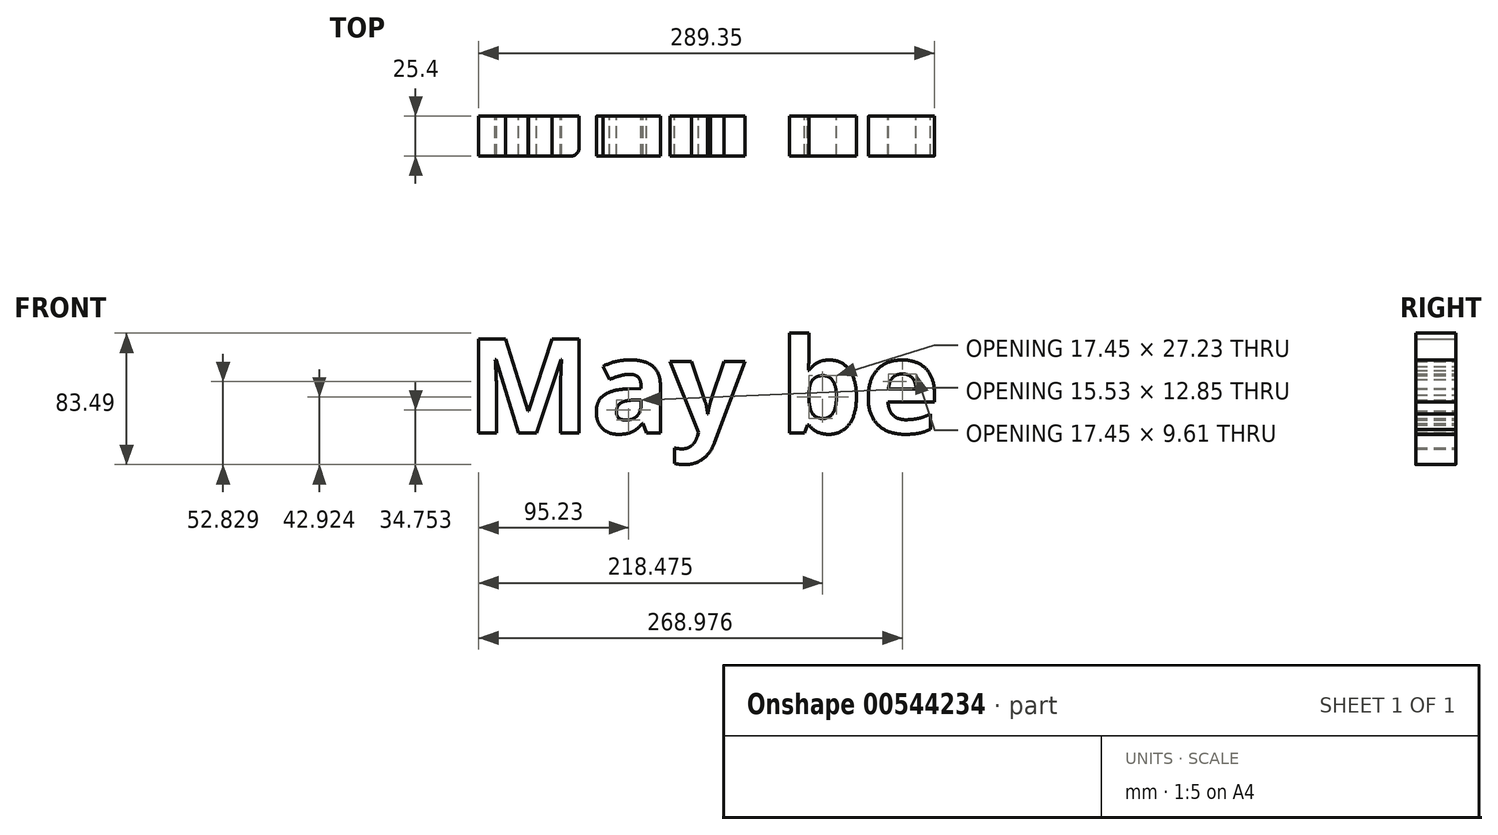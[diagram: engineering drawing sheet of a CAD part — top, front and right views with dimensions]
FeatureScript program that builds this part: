
annotation { "Feature Type Name" : "Feature", "Feature Type Description" : "" }
export const myFeature = defineFeature(function(context is Context, id is Id, definition is map)
    precondition{}
    {
        {
            var Q0;
            Q0=qCreatedBy(makeId("Front.planeOp"),FACE);
            var sketch = newSketch(context, id + "F0", { "sketchPlane" : qUnion([Q0])});
            skText(sketch, "E0", { "text": "May be", "fontName": "OpenSans-Bold.ttf"});
            const initialGuessF0  = {"E0": [-0.17978, -0.05261, 1, 0, 0.0601]};
            skSetInitialGuess(sketch, initialGuessF0);
            skSolve(sketch);
        }
        {
            var Q0;
            Q0 = qSketchRegion(id + "F0", true);
            extrude(context, id + "F1", {"entities" : qUnion([Q0]), "depth" : 25.4 * mm, "offsetDistance" : 25.4 * mm});
        }
        {
            var Q0;
            Q0=makeQuery(id+"F1.opExtrude","CAP_EDGE",EDGE,{"disambiguationData":[OSD([sQuery(id+"F0.wireOp",EDGE,"E0.sketch_text.stroke-11")])],"isStart":false});
            fillet(context, id + "F2", {"entities" : qUnion([Q0]), "radius" : 5.08 * mm, "tangentPropagation" : true, "allowEdgeOverflow" : false});
        }
    });
